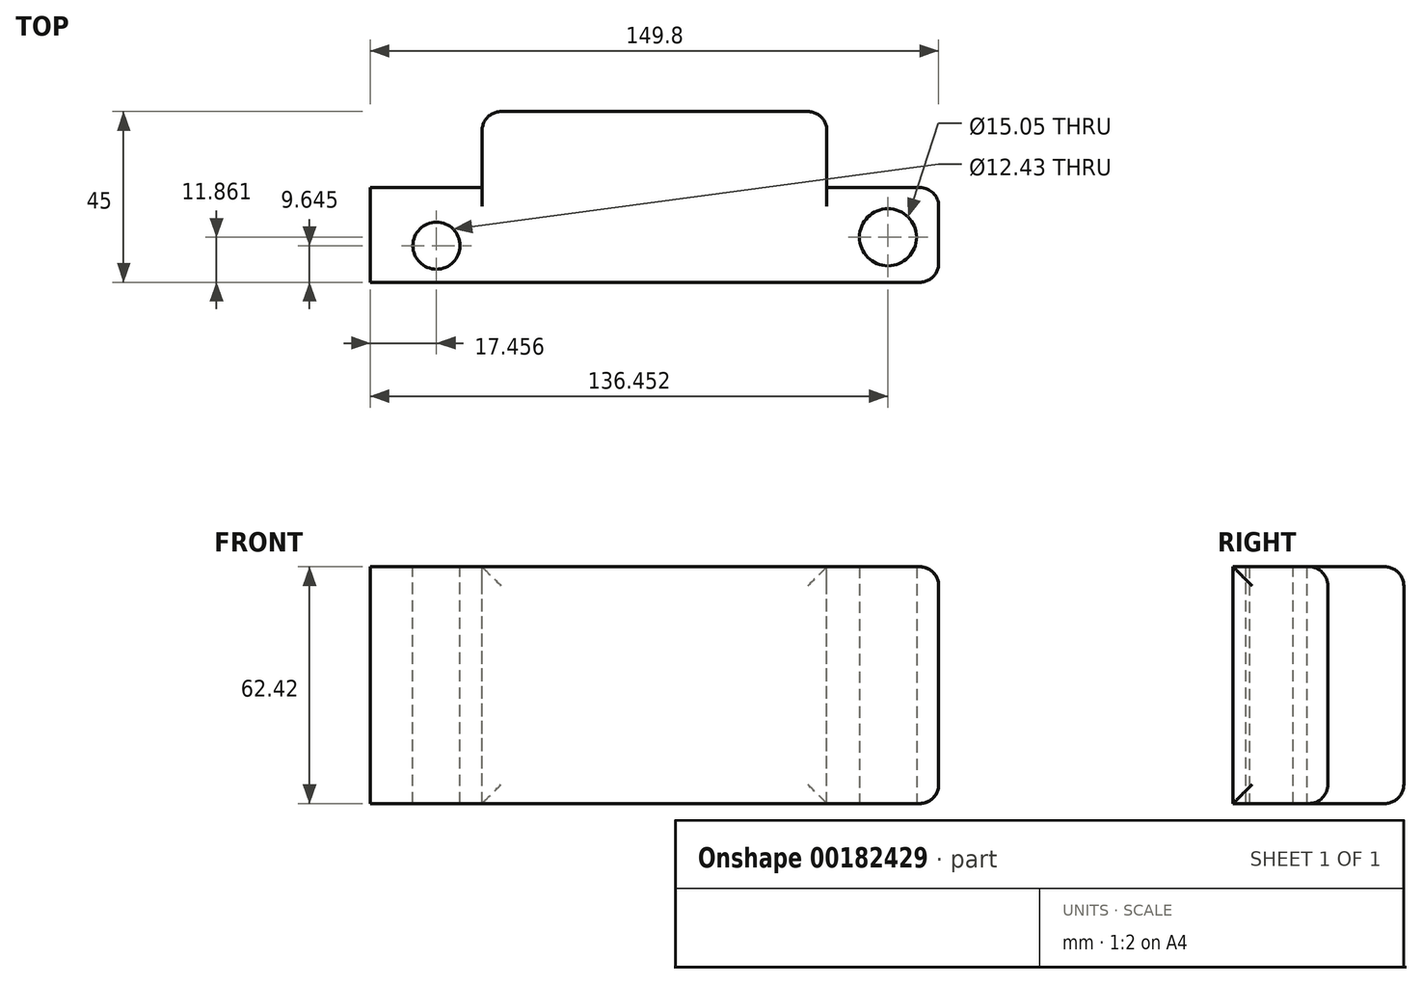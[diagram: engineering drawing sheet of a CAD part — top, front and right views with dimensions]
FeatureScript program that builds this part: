
annotation { "Feature Type Name" : "Feature", "Feature Type Description" : "" }
export const myFeature = defineFeature(function(context is Context, id is Id, definition is map)
    precondition{}
    {
        {
            var Q0;
            Q0=qCreatedBy(makeId("Front.planeOp"),FACE);
            var sketch = newSketch(context, id + "F0", { "sketchPlane" : qUnion([Q0])});
            skLineSegment(sketch, "E0.bottom", {"start": v(74.9, -31.2) * mm, "end": v(-74.9, -31.2) * mm});
            skLineSegment(sketch, "E0.top", {"start": v(74.9, 31.2) * mm, "end": v(-74.9, 31.2) * mm});
            skLineSegment(sketch, "E0.left", {"start": v(74.9, -31.2) * mm, "end": v(74.9, 31.2) * mm});
            skLineSegment(sketch, "E0.right", {"start": v(-74.9, -31.2) * mm, "end": v(-74.9, 31.2) * mm});
            skPoint(sketch, "E0.middle", {"position": v(0, 0) * mm});
            skSolve(sketch);
        }
        {
            var Q0;
            Q0=makeQuery(id+"F0.imprint","IMPRINT",FACE,{"disambiguationData":[TD([[makeQuery(id+"F0.imprint","IMPRINT",EDGE,{"derivedFrom":sQuery(id+"F0.wireOp",EDGE,"E0.bottom")}),-1.0]])]});
            extrude(context, id + "F1", {"entities" : qUnion([Q0]), "depth" : 25 * mm});
        }
        {
            var Q0;
            Q0=makeQuery(id+"F1.opExtrude","CAP_FACE",FACE,{"disambiguationData":[OSD([sQuery(id+"F0.wireOp",EDGE,"E0.bottom"),sQuery(id+"F0.wireOp",EDGE,"E0.top"),sQuery(id+"F0.wireOp",EDGE,"E0.left"),sQuery(id+"F0.wireOp",EDGE,"E0.right")])],"isStart":true});
            var sketch = newSketch(context, id + "F2", { "sketchPlane" : qUnion([Q0])});
            skLineSegment(sketch, "E1.bottom", {"start": v(45.43, -31.2) * mm, "end": v(-45.43, -31.2) * mm});
            skLineSegment(sketch, "E1.top", {"start": v(45.43, 31.2) * mm, "end": v(-45.43, 31.2) * mm});
            skLineSegment(sketch, "E1.left", {"start": v(45.43, -31.2) * mm, "end": v(45.43, 31.2) * mm});
            skLineSegment(sketch, "E1.right", {"start": v(-45.43, -31.2) * mm, "end": v(-45.43, 31.2) * mm});
            skPoint(sketch, "E1.middle", {"position": v(0, 0) * mm});
            skSolve(sketch);
        }
        {
            var Q0;
            Q0=makeQuery(id+"F2.imprint","IMPRINT",FACE,{"disambiguationData":[TD([[makeQuery(id+"F2.imprint","IMPRINT",EDGE,{"derivedFrom":sQuery(id+"F2.wireOp",EDGE,"E1.bottom")}),1.0]])]});
            extrude(context, id + "F3", {"entities" : qUnion([Q0]), "operationType" : NewBodyOperationType.ADD, "depth" : 20 * mm});
        }
        {
            var Q0;
            Q0=makeQuery(id+"F3.boolean.opBoolean","MERGE",FACE,{"derivedFrom":[makeQuery(id+"F1.opExtrude","SWEPT_FACE",FACE,{"disambiguationData":[OSD([sQuery(id+"F0.wireOp",EDGE,"E0.bottom")])]}),makeQuery(id+"F3.opExtrude","SWEPT_FACE",FACE,{"disambiguationData":[OSD([sQuery(id+"F2.wireOp",EDGE,"E1.bottom")])]})]});
            var sketch = newSketch(context, id + "F4", { "sketchPlane" : qUnion([Q0])});
            skCircle(sketch, "E2", {"center": v(61.55, 13.14) * mm, "radius": 7.52 * mm});
            skPoint(sketch, "E2.first.point", {"position": v(68.02, 16.97) * mm});
            skPoint(sketch, "E2.second.point", {"position": v(54.03, 13) * mm});
            skPoint(sketch, "E2.third.point", {"position": v(55.25, 9.03) * mm});
            skSolve(sketch);
        }
        {
            var Q0;
            Q0 = qSketchRegion(id + "F4", true);
            extrude(context, id + "F5", {"entities" : qUnion([Q0]), "operationType" : NewBodyOperationType.REMOVE, "oppositeDirection" : true, "depth" : 100 * mm});
        }
        {
            var Q0;
            Q0=makeQuery(id+"F3.boolean.opBoolean","MERGE",FACE,{"derivedFrom":[makeQuery(id+"F1.opExtrude","SWEPT_FACE",FACE,{"disambiguationData":[OSD([sQuery(id+"F0.wireOp",EDGE,"E0.top")])]}),makeQuery(id+"F3.opExtrude","SWEPT_FACE",FACE,{"disambiguationData":[OSD([sQuery(id+"F2.wireOp",EDGE,"E1.top")])]})]});
            var sketch = newSketch(context, id + "F6", { "sketchPlane" : qUnion([Q0])});
            skCircle(sketch, "E3", {"center": v(-57.44, -15.36) * mm, "radius": 6.22 * mm});
            skPoint(sketch, "E3.first.point", {"position": v(-55.05, -9.62) * mm});
            skPoint(sketch, "E3.second.point", {"position": v(-63.18, -17.75) * mm});
            skPoint(sketch, "E3.third.point", {"position": v(-54.02, -10.17) * mm});
            skSolve(sketch);
        }
        {
            var Q0;
            Q0 = qSketchRegion(id + "F6", true);
            extrude(context, id + "F7", {"entities" : qUnion([Q0]), "operationType" : NewBodyOperationType.REMOVE, "oppositeDirection" : true, "depth" : 100 * mm});
        }
        {
            var Q0;
            Q0=makeQuery(id+"F3.opExtrude","CAP_EDGE",EDGE,{"disambiguationData":[OSD([sQuery(id+"F2.wireOp",EDGE,"E1.right")])],"isStart":false});
            var Q1;
            Q1=makeQuery(id+"F3.opExtrude","CAP_EDGE",EDGE,{"disambiguationData":[OSD([sQuery(id+"F2.wireOp",EDGE,"E1.left")])],"isStart":false});
            var Q2;
            Q2=makeQuery(id+"F1.opExtrude","SWEPT_FACE",FACE,{"disambiguationData":[OSD([sQuery(id+"F0.wireOp",EDGE,"E0.left")])]});
            var Q3;
            Q3=makeQuery(id+"F3.opExtrude","CAP_EDGE",EDGE,{"disambiguationData":[OSD([sQuery(id+"F2.wireOp",EDGE,"E1.top")])],"isStart":false});
            var Q4;
            Q4=makeQuery(id+"F3.opExtrude","CAP_EDGE",EDGE,{"disambiguationData":[OSD([sQuery(id+"F2.wireOp",EDGE,"E1.bottom")])],"isStart":false});
            fillet(context, id + "F8", {"entities" : qUnion([Q0, Q1, Q2, Q3, Q4]), "radius" : 5 * mm, "tangentPropagation" : true, "allowEdgeOverflow" : false});
        }
        {
            var Q0;
            {var subQ0=sQuery(id+"F0.wireOp",EDGE,"E0.left");var subQ1=sQuery(id+"F0.wireOp",EDGE,"E0.bottom");Q0=makeQuery(id+"F3.boolean.opBoolean","SPLIT",EDGE,{"disambiguationData":[TD([makeQuery(id+"F1.opExtrude","SWEPT_FACE",FACE,{"disambiguationData":[OSD([subQ0])]})])],"derivedFrom":makeQuery(id+"F1.opExtrude","CAP_EDGE",EDGE,{"disambiguationData":[OSD([subQ1])],"isStart":true})});}
            var Q1;
            {var subQ0=sQuery(id+"F0.wireOp",EDGE,"E0.left");var subQ1=sQuery(id+"F0.wireOp",EDGE,"E0.top");Q1=makeQuery(id+"F3.boolean.opBoolean","SPLIT",EDGE,{"disambiguationData":[TD([makeQuery(id+"F1.opExtrude","SWEPT_FACE",FACE,{"disambiguationData":[OSD([subQ0])]})])],"derivedFrom":makeQuery(id+"F1.opExtrude","CAP_EDGE",EDGE,{"disambiguationData":[OSD([subQ1])],"isStart":true})});}
            fillet(context, id + "F9", {"entities" : qUnion([Q0, Q1]), "radius" : 5 * mm, "tangentPropagation" : true, "allowEdgeOverflow" : false});
        }
        {
            var Q0;
            {var subQ0=sQuery(id+"F0.wireOp",EDGE,"E0.right");var subQ1=sQuery(id+"F0.wireOp",EDGE,"E0.bottom");Q0=makeQuery(id+"F3.boolean.opBoolean","SPLIT",EDGE,{"disambiguationData":[TD([makeQuery(id+"F1.opExtrude","SWEPT_FACE",FACE,{"disambiguationData":[OSD([subQ0])]})])],"derivedFrom":makeQuery(id+"F1.opExtrude","CAP_EDGE",EDGE,{"disambiguationData":[OSD([subQ1])],"isStart":true})});}
            var Q1;
            {var subQ0=sQuery(id+"F0.wireOp",EDGE,"E0.right");var subQ1=sQuery(id+"F0.wireOp",EDGE,"E0.top");Q1=makeQuery(id+"F3.boolean.opBoolean","SPLIT",EDGE,{"disambiguationData":[TD([makeQuery(id+"F1.opExtrude","SWEPT_FACE",FACE,{"disambiguationData":[OSD([subQ0])]})])],"derivedFrom":makeQuery(id+"F1.opExtrude","CAP_EDGE",EDGE,{"disambiguationData":[OSD([subQ1])],"isStart":true})});}
            fillet(context, id + "F10", {"entities" : qUnion([Q0, Q1]), "radius" : 5 * mm, "tangentPropagation" : true, "allowEdgeOverflow" : false});
        }
    });
